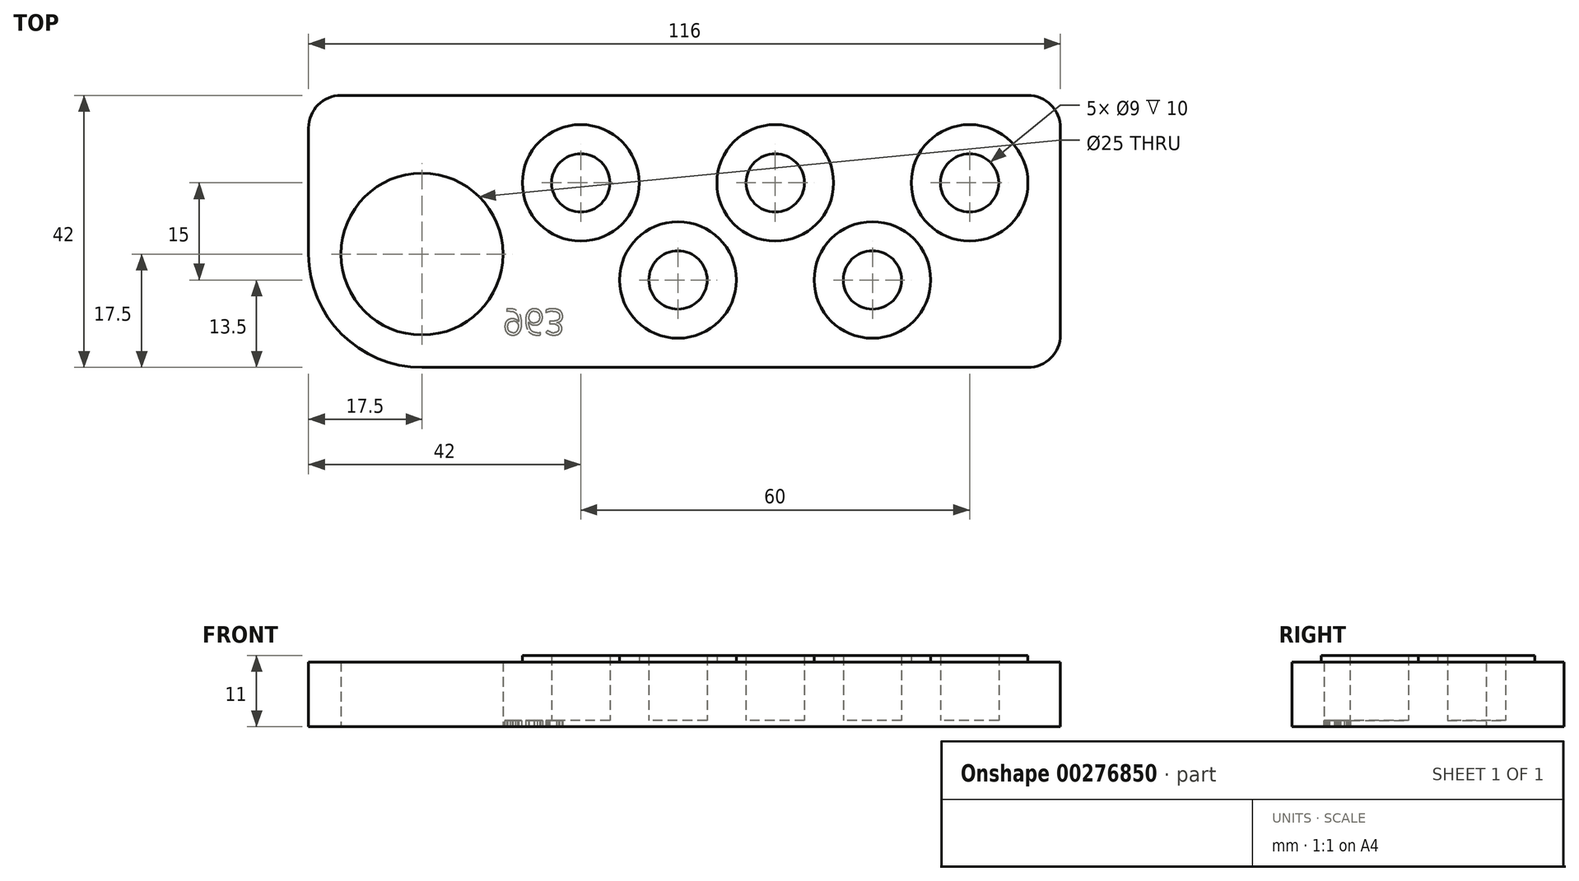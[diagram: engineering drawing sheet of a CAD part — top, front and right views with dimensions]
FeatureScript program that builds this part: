
annotation { "Feature Type Name" : "Feature", "Feature Type Description" : "" }
export const myFeature = defineFeature(function(context is Context, id is Id, definition is map)
    precondition{}
    {
        {
            var Q0;
            Q0=qCreatedBy(makeId("Top.planeOp"),FACE);
            var sketch = newSketch(context, id + "F0", { "sketchPlane" : qUnion([Q0])});
            skLineSegment(sketch, "E0.bottom", {"start": v(17.5, 0) * mm, "end": v(111, 0) * mm});
            skLineSegment(sketch, "E0.top", {"start": v(5, 42) * mm, "end": v(111, 42) * mm});
            skLineSegment(sketch, "E0.left", {"start": v(0, 17.5) * mm, "end": v(0, 37) * mm});
            skLineSegment(sketch, "E0.right", {"start": v(116, 5) * mm, "end": v(116, 37) * mm});
            skLineSegment(sketch, "E1.bottom", {"start": v(0, 0) * mm, "end": v(17.5, 0) * mm, "construction": true});
            skLineSegment(sketch, "E1.top", {"start": v(0, 17.5) * mm, "end": v(17.5, 17.5) * mm, "construction": true});
            skLineSegment(sketch, "E1.left", {"start": v(0, 0) * mm, "end": v(0, 17.5) * mm, "construction": true});
            skLineSegment(sketch, "E1.right", {"start": v(17.5, 0) * mm, "end": v(17.5, 17.5) * mm, "construction": true});
            skCircle(sketch, "E2", {"center": v(17.5, 17.5) * mm, "radius": 12.5 * mm});
            skPoint(sketch, "E3.visualSharp", {"position": v(0, 0) * mm});
            skArc(sketch, "E3.filletArc", {"start": v(0, 17.5) * mm, "mid": v(5.13, 5.13) * mm, "end": v(17.5, 0) * mm});
            skPoint(sketch, "E4.visualSharp", {"position": v(0, 42) * mm});
            skArc(sketch, "E4.filletArc", {"start": v(5, 42) * mm, "mid": v(1.46, 40.54) * mm, "end": v(0, 37) * mm});
            skPoint(sketch, "E5.visualSharp", {"position": v(116, 42) * mm});
            skArc(sketch, "E5.filletArc", {"start": v(116, 37) * mm, "mid": v(114.54, 40.54) * mm, "end": v(111, 42) * mm});
            skPoint(sketch, "E6.visualSharp", {"position": v(116, 0) * mm});
            skArc(sketch, "E6.filletArc", {"start": v(111, 0) * mm, "mid": v(114.54, 1.46) * mm, "end": v(116, 5) * mm});
            skSolve(sketch);
        }
        {
            var Q0;
            Q0=makeQuery(id+"F0.imprint","IMPRINT",FACE,{"disambiguationData":[TD([[makeQuery(id+"F0.imprint","IMPRINT",EDGE,{"derivedFrom":sQuery(id+"F0.wireOp",EDGE,"E0.bottom")}),1.0]])]});
            extrude(context, id + "F1", {"entities" : qUnion([Q0]), "depth" : 10 * mm});
        }
        {
            var Q0;
            Q0=makeQuery(id+"F1.opExtrude","CAP_FACE",FACE,{"disambiguationData":[OSD([sQuery(id+"F0.wireOp",EDGE,"E0.bottom"),sQuery(id+"F0.wireOp",EDGE,"E0.top"),sQuery(id+"F0.wireOp",EDGE,"E0.right"),sQuery(id+"F0.wireOp",EDGE,"E2"),sQuery(id+"F0.wireOp",EDGE,"E3.filletArc"),sQuery(id+"F0.wireOp",EDGE,"E4.filletArc"),sQuery(id+"F0.wireOp",EDGE,"E5.filletArc"),sQuery(id+"F0.wireOp",EDGE,"E6.filletArc")])],"isStart":false});
            var sketch = newSketch(context, id + "F2", { "sketchPlane" : qUnion([Q0])});
            skLineSegment(sketch, "E7.bottom", {"start": v(0, 0) * mm, "end": v(42, 0) * mm, "construction": true});
            skLineSegment(sketch, "E7.top", {"start": v(0, 28.5) * mm, "end": v(42, 28.5) * mm, "construction": true});
            skLineSegment(sketch, "E7.left", {"start": v(0, 0) * mm, "end": v(0, 28.5) * mm, "construction": true});
            skLineSegment(sketch, "E7.right", {"start": v(42, 0) * mm, "end": v(42, 28.5) * mm, "construction": true});
            skCircle(sketch, "E8", {"center": v(42, 28.5) * mm, "radius": 9 * mm});
            skLineSegment(sketch, "E9.bottom", {"start": v(42, 28.5) * mm, "end": v(57, 28.5) * mm, "construction": true});
            skLineSegment(sketch, "E9.top", {"start": v(42, 13.5) * mm, "end": v(57, 13.5) * mm, "construction": true});
            skLineSegment(sketch, "E9.left", {"start": v(42, 28.5) * mm, "end": v(42, 13.5) * mm, "construction": true});
            skLineSegment(sketch, "E9.right", {"start": v(57, 28.5) * mm, "end": v(57, 13.5) * mm, "construction": true});
            skCircle(sketch, "E10", {"center": v(57, 13.5) * mm, "radius": 9 * mm});
            skLineSegment(sketch, "E11.bottom", {"start": v(57, 28.5) * mm, "end": v(72, 28.5) * mm, "construction": true});
            skLineSegment(sketch, "E11.top", {"start": v(57, 13.5) * mm, "end": v(72, 13.5) * mm, "construction": true});
            skLineSegment(sketch, "E11.right", {"start": v(72, 28.5) * mm, "end": v(72, 13.5) * mm, "construction": true});
            skLineSegment(sketch, "E12.bottom", {"start": v(72, 28.5) * mm, "end": v(87, 28.5) * mm, "construction": true});
            skLineSegment(sketch, "E12.top", {"start": v(72, 13.5) * mm, "end": v(87, 13.5) * mm, "construction": true});
            skLineSegment(sketch, "E12.right", {"start": v(87, 28.5) * mm, "end": v(87, 13.5) * mm, "construction": true});
            skLineSegment(sketch, "E13.bottom", {"start": v(87, 28.5) * mm, "end": v(102, 28.5) * mm, "construction": true});
            skLineSegment(sketch, "E13.top", {"start": v(87, 13.5) * mm, "end": v(102, 13.5) * mm, "construction": true});
            skLineSegment(sketch, "E13.right", {"start": v(102, 28.5) * mm, "end": v(102, 13.5) * mm, "construction": true});
            skCircle(sketch, "E14", {"center": v(72, 28.5) * mm, "radius": 9 * mm});
            skCircle(sketch, "E15", {"center": v(87, 13.5) * mm, "radius": 9 * mm});
            skCircle(sketch, "E16", {"center": v(102, 28.5) * mm, "radius": 9 * mm});
            skCircle(sketch, "E17", {"center": v(42, 28.5) * mm, "radius": 4.5 * mm});
            skCircle(sketch, "E18", {"center": v(57, 13.5) * mm, "radius": 4.5 * mm});
            skCircle(sketch, "E19", {"center": v(72, 28.5) * mm, "radius": 4.5 * mm});
            skCircle(sketch, "E20", {"center": v(87, 13.5) * mm, "radius": 4.5 * mm});
            skCircle(sketch, "E21", {"center": v(102, 28.5) * mm, "radius": 4.5 * mm});
            skSolve(sketch);
        }
        {
            var Q0;
            Q0=makeQuery(id+"F2.imprint","IMPRINT",FACE,{"disambiguationData":[TD([[makeQuery(id+"F2.imprint","IMPRINT",EDGE,{"derivedFrom":sQuery(id+"F2.wireOp",EDGE,"E8")}),1.0]])]});
            var Q1;
            Q1=makeQuery(id+"F2.imprint","IMPRINT",FACE,{"disambiguationData":[TD([[makeQuery(id+"F2.imprint","IMPRINT",EDGE,{"derivedFrom":sQuery(id+"F2.wireOp",EDGE,"E10")}),1.0]])]});
            var Q2;
            Q2=makeQuery(id+"F2.imprint","IMPRINT",FACE,{"disambiguationData":[TD([[makeQuery(id+"F2.imprint","IMPRINT",EDGE,{"derivedFrom":sQuery(id+"F2.wireOp",EDGE,"E14")}),1.0]])]});
            var Q3;
            Q3=makeQuery(id+"F2.imprint","IMPRINT",FACE,{"disambiguationData":[TD([[makeQuery(id+"F2.imprint","IMPRINT",EDGE,{"derivedFrom":sQuery(id+"F2.wireOp",EDGE,"E15")}),1.0]])]});
            var Q4;
            Q4=makeQuery(id+"F2.imprint","IMPRINT",FACE,{"disambiguationData":[TD([[makeQuery(id+"F2.imprint","IMPRINT",EDGE,{"derivedFrom":sQuery(id+"F2.wireOp",EDGE,"E16")}),1.0]])]});
            extrude(context, id + "F3", {"entities" : qUnion([Q0, Q1, Q2, Q3, Q4]), "operationType" : NewBodyOperationType.ADD, "depth" : 1 * mm});
        }
        {
            var Q0;
            Q0=makeQuery(id+"F3.boolean.opBoolean","SPLIT",FACE,{"disambiguationData":[TD([makeQuery(id+"F3.opExtrude","SWEPT_FACE",FACE,{"disambiguationData":[OSD([sQuery(id+"F2.wireOp",EDGE,"E17")])]})])],"derivedFrom":makeQuery(id+"F1.opExtrude","CAP_FACE",FACE,{"disambiguationData":[OSD([sQuery(id+"F0.wireOp",EDGE,"E0.bottom"),sQuery(id+"F0.wireOp",EDGE,"E0.top"),sQuery(id+"F0.wireOp",EDGE,"E0.right"),sQuery(id+"F0.wireOp",EDGE,"E2"),sQuery(id+"F0.wireOp",EDGE,"E3.filletArc"),sQuery(id+"F0.wireOp",EDGE,"E4.filletArc"),sQuery(id+"F0.wireOp",EDGE,"E5.filletArc"),sQuery(id+"F0.wireOp",EDGE,"E6.filletArc")])],"isStart":false})});
            var Q1;
            Q1=makeQuery(id+"F3.boolean.opBoolean","SPLIT",FACE,{"disambiguationData":[TD([makeQuery(id+"F3.opExtrude","SWEPT_FACE",FACE,{"disambiguationData":[OSD([sQuery(id+"F2.wireOp",EDGE,"E18")])]})])],"derivedFrom":makeQuery(id+"F1.opExtrude","CAP_FACE",FACE,{"disambiguationData":[OSD([sQuery(id+"F0.wireOp",EDGE,"E0.bottom"),sQuery(id+"F0.wireOp",EDGE,"E0.top"),sQuery(id+"F0.wireOp",EDGE,"E0.right"),sQuery(id+"F0.wireOp",EDGE,"E2"),sQuery(id+"F0.wireOp",EDGE,"E3.filletArc"),sQuery(id+"F0.wireOp",EDGE,"E4.filletArc"),sQuery(id+"F0.wireOp",EDGE,"E5.filletArc"),sQuery(id+"F0.wireOp",EDGE,"E6.filletArc")])],"isStart":false})});
            var Q2;
            Q2=makeQuery(id+"F3.boolean.opBoolean","SPLIT",FACE,{"disambiguationData":[TD([makeQuery(id+"F3.opExtrude","SWEPT_FACE",FACE,{"disambiguationData":[OSD([sQuery(id+"F2.wireOp",EDGE,"E19")])]})])],"derivedFrom":makeQuery(id+"F1.opExtrude","CAP_FACE",FACE,{"disambiguationData":[OSD([sQuery(id+"F0.wireOp",EDGE,"E0.bottom"),sQuery(id+"F0.wireOp",EDGE,"E0.top"),sQuery(id+"F0.wireOp",EDGE,"E0.right"),sQuery(id+"F0.wireOp",EDGE,"E2"),sQuery(id+"F0.wireOp",EDGE,"E3.filletArc"),sQuery(id+"F0.wireOp",EDGE,"E4.filletArc"),sQuery(id+"F0.wireOp",EDGE,"E5.filletArc"),sQuery(id+"F0.wireOp",EDGE,"E6.filletArc")])],"isStart":false})});
            var Q3;
            Q3=makeQuery(id+"F3.boolean.opBoolean","SPLIT",FACE,{"disambiguationData":[TD([makeQuery(id+"F3.opExtrude","SWEPT_FACE",FACE,{"disambiguationData":[OSD([sQuery(id+"F2.wireOp",EDGE,"E20")])]})])],"derivedFrom":makeQuery(id+"F1.opExtrude","CAP_FACE",FACE,{"disambiguationData":[OSD([sQuery(id+"F0.wireOp",EDGE,"E0.bottom"),sQuery(id+"F0.wireOp",EDGE,"E0.top"),sQuery(id+"F0.wireOp",EDGE,"E0.right"),sQuery(id+"F0.wireOp",EDGE,"E2"),sQuery(id+"F0.wireOp",EDGE,"E3.filletArc"),sQuery(id+"F0.wireOp",EDGE,"E4.filletArc"),sQuery(id+"F0.wireOp",EDGE,"E5.filletArc"),sQuery(id+"F0.wireOp",EDGE,"E6.filletArc")])],"isStart":false})});
            var Q4;
            Q4=makeQuery(id+"F3.boolean.opBoolean","SPLIT",FACE,{"disambiguationData":[TD([makeQuery(id+"F3.opExtrude","SWEPT_FACE",FACE,{"disambiguationData":[OSD([sQuery(id+"F2.wireOp",EDGE,"E21")])]})])],"derivedFrom":makeQuery(id+"F1.opExtrude","CAP_FACE",FACE,{"disambiguationData":[OSD([sQuery(id+"F0.wireOp",EDGE,"E0.bottom"),sQuery(id+"F0.wireOp",EDGE,"E0.top"),sQuery(id+"F0.wireOp",EDGE,"E0.right"),sQuery(id+"F0.wireOp",EDGE,"E2"),sQuery(id+"F0.wireOp",EDGE,"E3.filletArc"),sQuery(id+"F0.wireOp",EDGE,"E4.filletArc"),sQuery(id+"F0.wireOp",EDGE,"E5.filletArc"),sQuery(id+"F0.wireOp",EDGE,"E6.filletArc")])],"isStart":false})});
            extrude(context, id + "F4", {"entities" : qUnion([Q0, Q1, Q2, Q3, Q4]), "operationType" : NewBodyOperationType.REMOVE, "oppositeDirection" : true, "depth" : 9 * mm});
        }
        {
            var Q0;
            Q0=makeQuery(id+"F1.opExtrude","CAP_FACE",FACE,{"disambiguationData":[OSD([sQuery(id+"F0.wireOp",EDGE,"E0.bottom"),sQuery(id+"F0.wireOp",EDGE,"E0.top"),sQuery(id+"F0.wireOp",EDGE,"E0.left"),sQuery(id+"F0.wireOp",EDGE,"E0.right"),sQuery(id+"F0.wireOp",EDGE,"E2"),sQuery(id+"F0.wireOp",EDGE,"E3.filletArc"),sQuery(id+"F0.wireOp",EDGE,"E4.filletArc"),sQuery(id+"F0.wireOp",EDGE,"E5.filletArc"),sQuery(id+"F0.wireOp",EDGE,"E6.filletArc")])],"isStart":true});
            var sketch = newSketch(context, id + "F5", { "sketchPlane" : qUnion([Q0])});
            skLineSegment(sketch, "E22.bottom", {"start": v(0, 0) * mm, "end": v(30, 0) * mm, "construction": true});
            skLineSegment(sketch, "E22.top", {"start": v(0, -5) * mm, "end": v(30, -5) * mm, "construction": true});
            skLineSegment(sketch, "E22.left", {"start": v(0, 0) * mm, "end": v(0, -5) * mm, "construction": true});
            skLineSegment(sketch, "E22.right", {"start": v(30, 0) * mm, "end": v(30, -5) * mm, "construction": true});
            skText(sketch, "E23", { "text": "963", "fontName": "OpenSans-Regular.ttf"});
            const initialGuessF5  = {"E23": [0.03, -0.009, 1, 0, 0.004]};
            skSetInitialGuess(sketch, initialGuessF5);
            skSolve(sketch);
        }
        {
            var Q0;
            Q0 = qSketchRegion(id + "F5", true);
            extrude(context, id + "F6", {"entities" : qUnion([Q0]), "operationType" : NewBodyOperationType.REMOVE, "oppositeDirection" : true, "depth" : 1 * mm});
        }
    });
